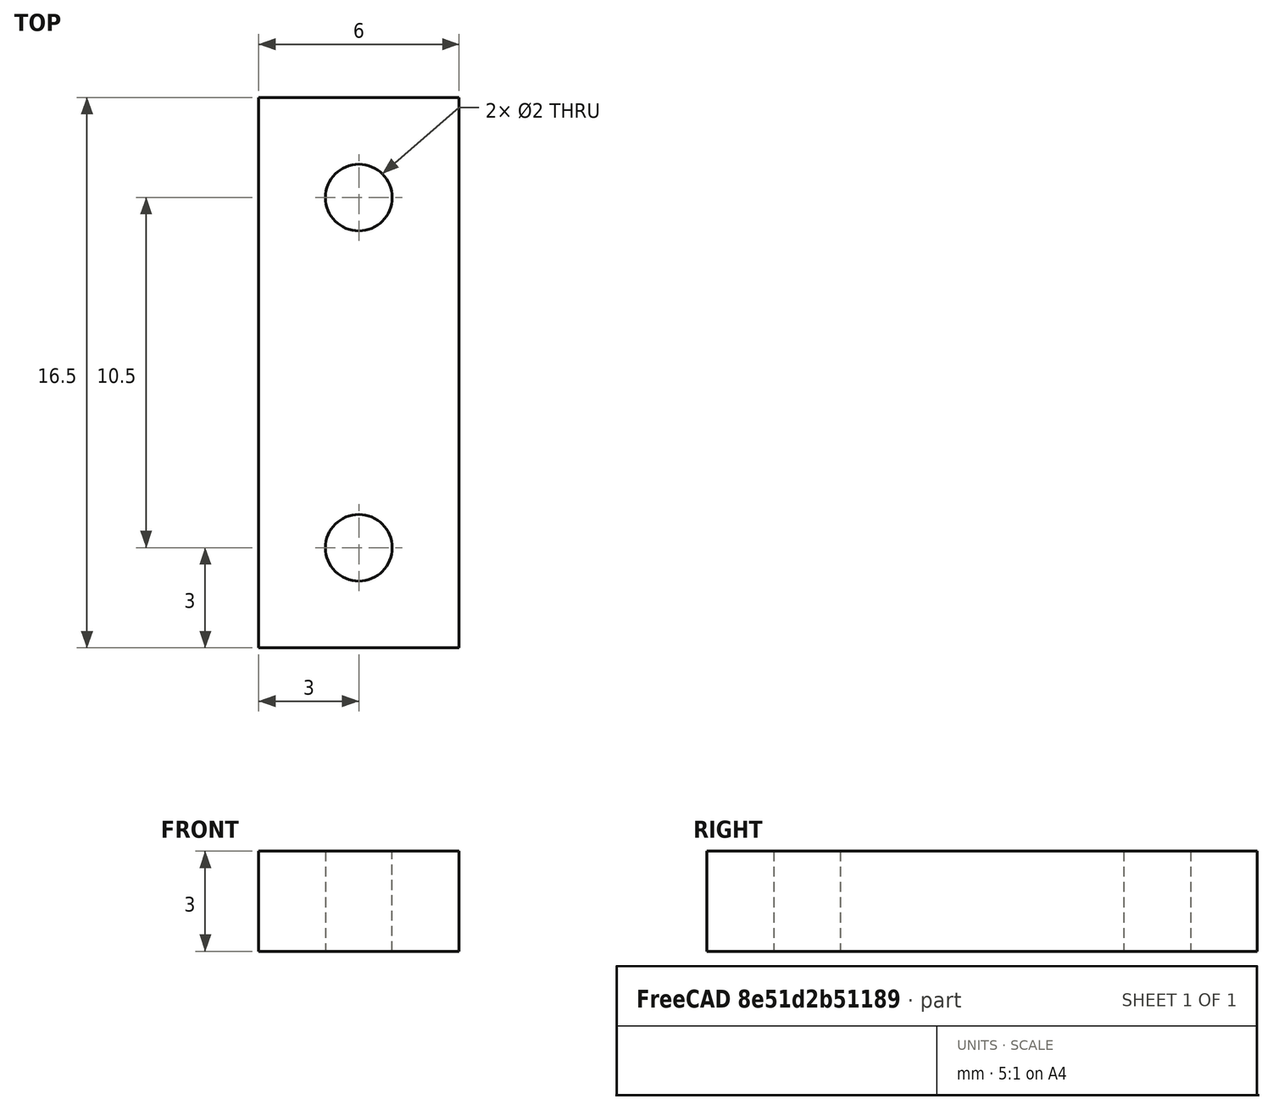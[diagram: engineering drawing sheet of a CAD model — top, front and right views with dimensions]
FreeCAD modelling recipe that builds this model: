
FCSTD DOCUMENT  (FreeCAD 0.19R24366 (Git))
Label: mdo-display-holder
License: All rights reserved
LicenseURL: http://en.wikipedia.org/wiki/All_rights_reserved
objects: Sketcher::SketchObject×1, PartDesign::Pad×1, PartDesign::Body×1, TechDraw::DrawSVGTemplate×1, TechDraw::DrawViewPart×1, TechDraw::DrawPage×1
note: 4 computed .brp shape members not serialized (recipe doc carries the construction recipe); baked Part::Feature solids carry a one-line shape summary decoded from their .brp

FEATURE [Sketcher::SketchObject] Sketch
  FullyConstrained = true
  MapMode = 5
  Support = -> [XY_Plane]
  sketch-geometry (6):
    g0: LineSegment StartX=0 StartY=0 StartZ=0 EndX=6 EndY=0 EndZ=0
    g1: LineSegment StartX=6 StartY=0 StartZ=0 EndX=6 EndY=16.5 EndZ=0
    g2: LineSegment StartX=6 StartY=16.5 StartZ=0 EndX=0 EndY=16.5 EndZ=0
    g3: LineSegment StartX=0 StartY=16.5 StartZ=0 EndX=0 EndY=0 EndZ=0
    g4: Circle CenterX=3 CenterY=3 CenterZ=0 NormalX=0 NormalY=0 NormalZ=1 AngleXU=0 Radius=1
    g5: Circle CenterX=3 CenterY=13.5 CenterZ=0 NormalX=0 NormalY=0 NormalZ=1 AngleXU=0 Radius=1
  constraints (17):
    c: Coincident(g0,g1)
    c: Coincident(g1,g2)
    c: Coincident(g2,g3)
    c: Coincident(g3,g0)
    c: Horizontal(g0)
    c: Horizontal(g2)
    c: Vertical(g1)
    c: Vertical(g3)
    c: Coincident(g0,g-1)
    c: DistanceX(g0,g0) = 6
    c: Diameter(g4) = 2
    c: DistanceX(g0,g4) = 3
    c: DistanceY(g0,g4) = 3
    c: Equal(g4,g5) = 2
    c: DistanceX(g4,g5) = 0
    c: DistanceY(g4,g5) = 10.5
    c: DistanceY(g5,g1) = 3
FEATURE [PartDesign::Pad] Pad
  Direction = (1,1,1)
  Length = 3
  Length2 = 100
  Profile = -> Sketch
  Type = 0
FEATURE [PartDesign::Body] Body
  Group = -> [Sketch,Pad]
  Origin = -> Origin
  Tip = -> Pad
FEATURE [TechDraw::DrawSVGTemplate] Template
  EditableTexts = Designed_by_Name=Designed by Name; Drawing_number=Drawing number; FC-Date=Date; FC-SC=Scale; FC-SH=Sheet; FC-Title=Title; Subtitle=Subtitle; Weight=Weight
  Height = 210
  Orientation = 1
  Width = 297
FEATURE [TechDraw::DrawViewPart] View
  CoarseView = false
  Direction = (0,0,-1)
  Focus = 100
  HardHidden = false
  IsoCount = 0
  IsoHidden = false
  IsoVisible = false
  LockPosition = false
  Perspective = false
  Rotation = 0
  ScaleType = 0
  SeamHidden = false
  SeamVisible = true
  SmoothHidden = false
  SmoothVisible = true
  Source = -> [Body]
  X = 148.5
  XDirection = (1,0,0)
  Y = 105
FEATURE [TechDraw::DrawPage] Page
  KeepUpdated = true
  NextBalloonIndex = 1
  ProjectionType = 0
  Template = -> Template
  Views = -> [View]
